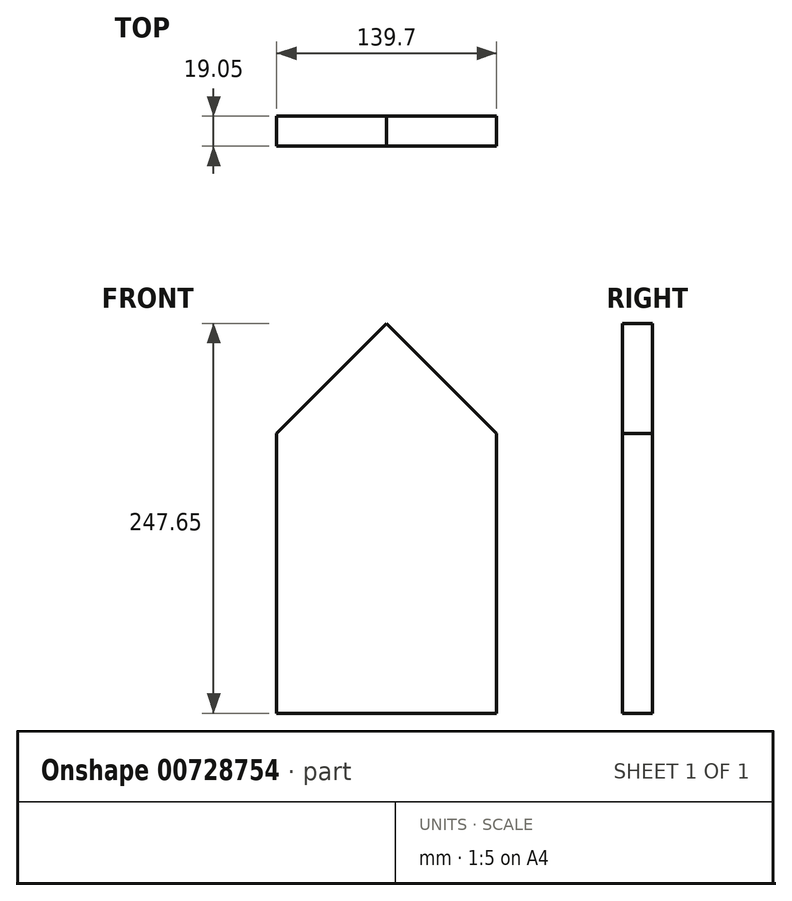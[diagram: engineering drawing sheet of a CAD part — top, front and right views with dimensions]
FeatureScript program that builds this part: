
annotation { "Feature Type Name" : "Feature", "Feature Type Description" : "" }
export const myFeature = defineFeature(function(context is Context, id is Id, definition is map)
    precondition{}
    {
        {
            var Q0;
            Q0=qCreatedBy(makeId("Front.planeOp"),FACE);
            var sketch = newSketch(context, id + "F0", { "sketchPlane" : qUnion([Q0])});
            skLineSegment(sketch, "E0.bottom", {"start": v(69.85, -88.9) * mm, "end": v(-69.85, -88.9) * mm});
            skLineSegment(sketch, "E0.left", {"start": v(69.85, -88.9) * mm, "end": v(69.85, 88.9) * mm});
            skLineSegment(sketch, "E0.right", {"start": v(-69.85, -88.9) * mm, "end": v(-69.85, 88.9) * mm});
            skPoint(sketch, "E0.middle", {"position": v(0, 0) * mm});
            skLineSegment(sketch, "E1", {"start": v(-69.85, 88.9) * mm, "end": v(0, 158.75) * mm});
            skLineSegment(sketch, "E2", {"start": v(0, 158.75) * mm, "end": v(69.85, 88.9) * mm});
            skSolve(sketch);
        }
        {
            var Q0;
            Q0=qSketchRegion(id+"F0",true);
            extrude(context, id + "F1", {"entities" : qUnion([Q0]), "depth" : 19.05 * mm, "offsetDistance" : 25.4 * mm});
        }
    });
